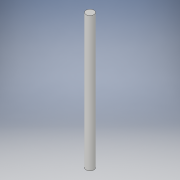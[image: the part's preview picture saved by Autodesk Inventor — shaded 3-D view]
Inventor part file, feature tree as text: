
AUTODESK INVENTOR PART (.ipt)
format: ipt  version: 2019 (Build 230136000, 136)  size: 89,088 bytes
history: native  units: in
note: dims shown in document units (in); Inventor stores cm internally (conversion verified against a paired STEP export)
features: extrude x1, sketch x1
ambient origin geometry x8: Origin, YZ Plane, XZ Plane, XY Plane, X Axis, Y Axis, Z Axis, Center Point
bodies: Solid1 (feature_tree)
feature tree (2):
  extrude  "Extrusion1"  Depth=4.25in TaperAngle=0.0deg
  sketch  "Sketch1"  dims[d0=0.25in d1=4.25in d2=0.0in]
